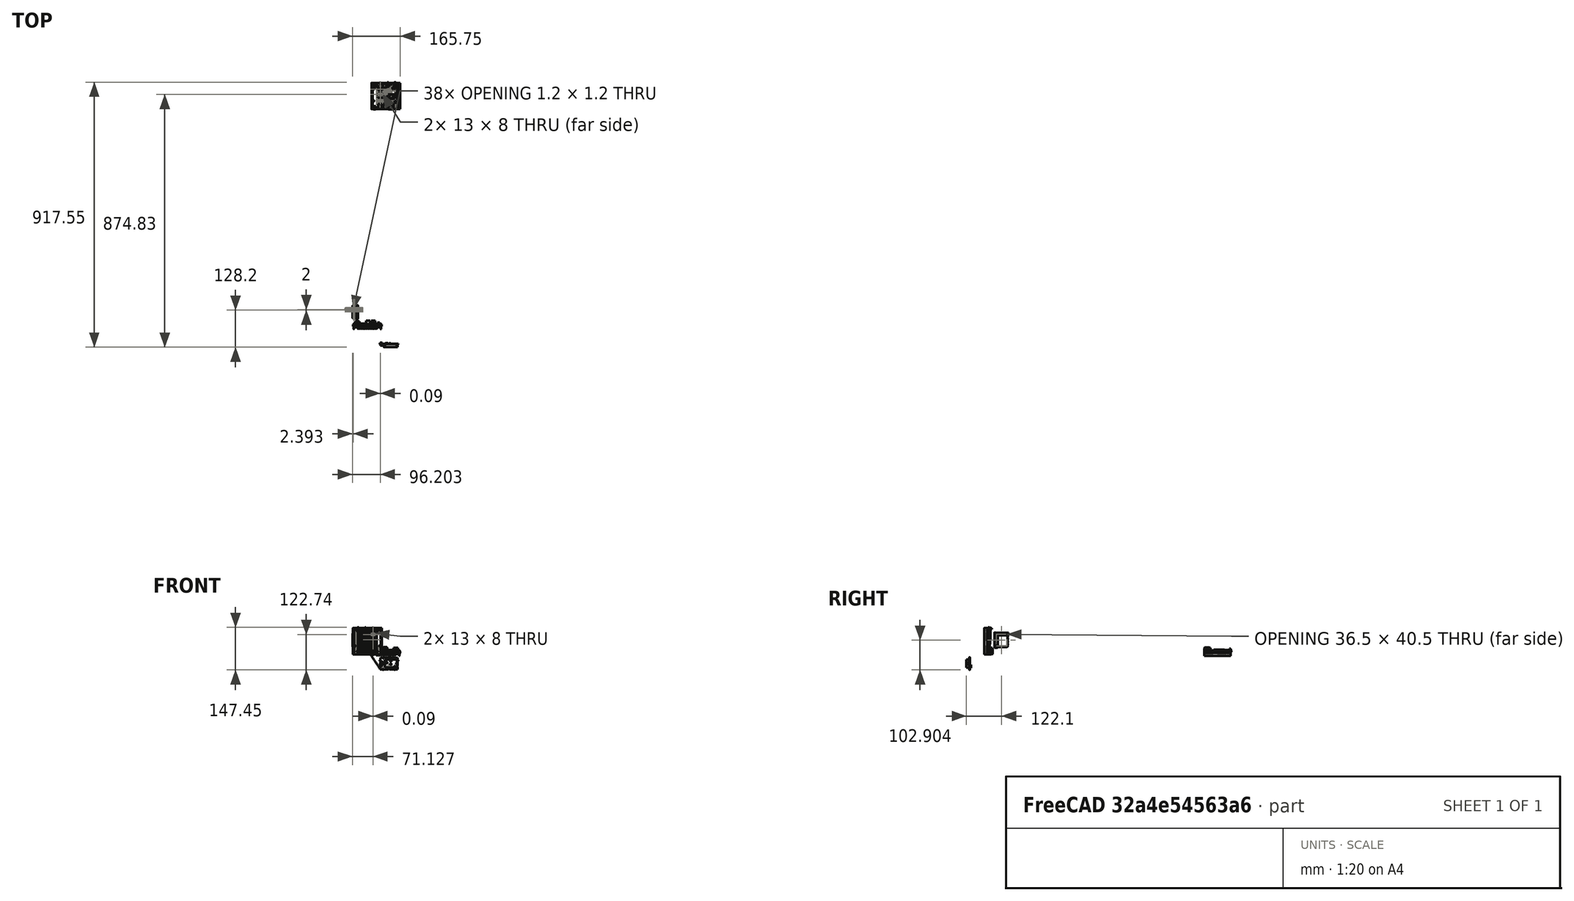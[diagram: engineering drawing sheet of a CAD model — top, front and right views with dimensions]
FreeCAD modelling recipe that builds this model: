
FCSTD DOCUMENT  (FreeCAD 0.20R29410 (Git))
Label: ISM
License: All rights reserved
LicenseURL: http://en.wikipedia.org/wiki/All_rights_reserved
objects: Part::Feature×29, Part::Cylinder×18, Part::MultiFuse×9, Part::Fillet×7, Part::Cut×6, Part::Extrusion×5, App::Part×4, Part::Box×3, Sketcher::SketchObject×3, Part::Part2DObjectPython×2
note: 82 computed .brp shape members not serialized (recipe doc carries the construction recipe); baked Part::Feature solids carry a one-line shape summary decoded from their .brp

FEATURE [Part::Box] Box001  label="Cube001"
  AttacherType = Attacher::AttachEngine3D
  Height = 0.1
  Length = 0.1
  Width = 0.1
FEATURE [Part::Feature] Part__Feature007  label="Heat Sink"
  shape: bbox 100 x 91 x 19 mm, 161 faces (baked)
FEATURE [Part::Feature] Part__Feature008  label="Battery Holder"
  shape: bbox 28.5 x 16 x 6 mm, 91 faces (baked)
FEATURE [Part::Feature] Part__Feature009  label="DC Jack"
  shape: bbox 7.6 x 11.5 x 9.75 mm, 10 faces (baked)
FEATURE [Part::Feature] Part__Feature010  label="PCB"
  shape: bbox 90 x 90 x 3.3 mm, 59 faces (baked)
FEATURE [Part::Feature] Part__Feature011  label="HDMI"
  shape: bbox 14.51 x 11.61 x 5.506 mm, 31 faces (baked)
FEATURE [Part::Feature] Part__Feature012  label="Ethernet"
  shape: bbox 15.9 x 21.4 x 13.5 mm, 25 faces (baked)
FEATURE [Part::Feature] Part__Feature013  label="USB 3.0 B"
  shape: bbox 14.55 x 17.5 x 16.15 mm, 36 faces (baked)
FEATURE [Part::Feature] Part__Feature014  label="USB 3.0 A"
  shape: bbox 14.55 x 17.5 x 16.15 mm, 36 faces (baked)
FEATURE [Part::Feature] Part__Feature015  label="Audio Jack"
  shape: bbox 6.5 x 14 x 4 mm, 10 faces (baked)
FEATURE [Part::Feature] Part__Feature016  label="Fan Plug"
  shape: bbox 3.75 x 7.5 x 4.75 mm, 32 faces (baked)
FEATURE [Part::Feature] Part__Feature017  label="REMOCON"
  shape: bbox 7.006 x 5.006 x 12.01 mm, 30 faces (baked)
FEATURE [Part::Feature] Part__Feature018  label="eMMC"
  shape: bbox 13.5 x 18.5 x 2.8 mm, 33 faces (baked)
FEATURE [Part::Feature] Part__Feature019  label="MicroUSB"
  shape: bbox 7.012 x 4.616 x 3.511 mm, 31 faces (baked)
FEATURE [Part::Feature] Part__Feature020  label="Switch"
  shape: bbox 9 x 5.74 x 3.5 mm, 11 faces (baked)
FEATURE [Part::Feature] Part__Feature021  label="MicroSD Card Socket"
  shape: bbox 11.5 x 5.5 x 3.5 mm, 11 faces (baked)
FEATURE [Part::Feature] Part__Feature022  label="7 Pin Header"
  shape: bbox 17.5 x 2.5 x 8 mm, 41 faces (baked)
FEATURE [Part::Feature] Part__Feature023  label="UART"
  shape: bbox 5 x 12.5 x 6 mm, 43 faces (baked)
FEATURE [Part::Feature] Part__Feature024  label="40 Pin Header"
  shape: bbox 5 x 50 x 8 mm, 206 faces (baked)
FEATURE [App::Part] Odroid_N2__v4  label="Odroid-N2+ v4"
  Group = -> [Part__Feature007,Part__Feature008,Part__Feature009,Part__Feature010,Part__Feature011,Part__Feature012,Part__Feature013,Part__Feature014,Part__Feature015,Part__Feature016,Part__Feature017,Part__Feature018,Part__Feature019,Part__Feature020,Part__Feature021,Part__Feature022,Part__Feature023,Part__Feature024]
  Origin = -> Origin002
  Placement = pos=(31,-814,-44.46) rot=(0,0,1;0rad)
FEATURE [Part::MultiFuse] Fusion001  label="odroidN2"
  Placement = pos=(5,50,52) rot=(0,0.707107,0.707107;3.14159rad)
  Shapes = -> [Box001,Odroid_N2__v4]
FEATURE [Sketcher::SketchObject] Sketch
  FullyConstrained = true
  sketch-geometry (28):
    g0: LineSegment StartX=-93.25 StartY=70.6 StartZ=0 EndX=-93.25 EndY=67.6 EndZ=0
    g1: LineSegment StartX=-93.25 StartY=67.6 StartZ=0 EndX=-95.25 EndY=67.6 EndZ=0
    g2: LineSegment StartX=-95.25 StartY=67.6 StartZ=0 EndX=-95.25 EndY=65.8 EndZ=0
    g3: LineSegment StartX=-95.25 StartY=65.8 StartZ=0 EndX=-93.25 EndY=65.8 EndZ=0
    g4: LineSegment StartX=-93.25 StartY=65.8 StartZ=0 EndX=-93.25 EndY=64.3 EndZ=0
    g5: LineSegment StartX=-93.25 StartY=64.3 StartZ=0 EndX=-95.25 EndY=64.3 EndZ=0
    g6: LineSegment StartX=-95.25 StartY=64.3 StartZ=0 EndX=-95.25 EndY=62.5 EndZ=0
    g7: LineSegment StartX=-95.25 StartY=62.5 StartZ=0 EndX=-93.25 EndY=62.5 EndZ=0
    g8: LineSegment StartX=-93.25 StartY=62.5 StartZ=0 EndX=-93.25 EndY=59.5 EndZ=0
    g9: LineSegment StartX=-93.25 StartY=59.5 StartZ=0 EndX=-97.25 EndY=59.5 EndZ=0
    g10: LineSegment StartX=-97.25 StartY=59.5 StartZ=0 EndX=-97.25 EndY=87.6 EndZ=0
    g11: LineSegment StartX=-97.25 StartY=87.6 StartZ=0 EndX=7.25 EndY=87.6 EndZ=0
    g12: LineSegment StartX=7.25 StartY=87.6 StartZ=0 EndX=7.25 EndY=59.5 EndZ=0
    g13: LineSegment StartX=7.25 StartY=59.5 StartZ=0 EndX=3.25 EndY=59.5 EndZ=0
    g14: LineSegment StartX=3.25 StartY=59.5 StartZ=0 EndX=3.25 EndY=62.5 EndZ=0
    g15: LineSegment StartX=3.25 StartY=62.5 StartZ=0 EndX=5.25 EndY=62.5 EndZ=0
    g16: LineSegment StartX=5.25 StartY=62.5 StartZ=0 EndX=5.25 EndY=64.3 EndZ=0
    g17: LineSegment StartX=5.25 StartY=64.3 StartZ=0 EndX=3.25 EndY=64.3 EndZ=0
    g18: LineSegment StartX=3.25 StartY=64.3 StartZ=0 EndX=3.25 EndY=65.8 EndZ=0
    g19: LineSegment StartX=3.25 StartY=65.8 StartZ=0 EndX=5.25 EndY=65.8 EndZ=0
    g20: LineSegment StartX=5.25 StartY=65.8 StartZ=0 EndX=5.25 EndY=67.6 EndZ=0
    g21: LineSegment StartX=5.25 StartY=67.6 StartZ=0 EndX=3.25 EndY=67.6 EndZ=0
    g22: LineSegment StartX=3.25 StartY=67.6 StartZ=0 EndX=3.25 EndY=70.6 EndZ=0
    g23: LineSegment StartX=3.25 StartY=70.6 StartZ=0 EndX=5.25 EndY=70.6 EndZ=0
    g24: LineSegment StartX=5.25 StartY=70.6 StartZ=0 EndX=5.25 EndY=85.6 EndZ=0
    g25: LineSegment StartX=5.25 StartY=85.6 StartZ=0 EndX=-95.25 EndY=85.6 EndZ=0
    g26: LineSegment StartX=-95.25 StartY=85.6 StartZ=0 EndX=-95.25 EndY=70.6 EndZ=0
    g27: LineSegment StartX=-95.25 StartY=70.6 StartZ=0 EndX=-93.25 EndY=70.6 EndZ=0
  constraints (84):
    c: Vertical(g0)
    c: Coincident(g1,g0)
    c: Horizontal(g3)
    c: Coincident(g6,g5)
    c: Coincident(g7,g6)
    c: Coincident(g8,g7)
    c: Vertical(g8)
    c: Coincident(g9,g8)
    c: Vertical(g10)
    c: Horizontal(g11)
    c: Vertical(g12)
    c: Coincident(g14,g13)
    c: Coincident(g16,g15)
    c: Vertical(g16)
    c: Coincident(g17,g16)
    c: Coincident(g20,g19)
    c: Vertical(g20)
    c: Coincident(g21,g20)
    c: Coincident(g22,g21)
    c: Horizontal(g25)
    c: Vertical(g26)
    c: Coincident(g27,g0)
    c: Horizontal(g27)
    c: Coincident(g11,g12)
    c: Horizontal(g9)
    c: Horizontal(g7)
    c: Horizontal(g5)
    c: Vertical(g6)
    c: Vertical(g4)
    c: Vertical(g2)
    c: Horizontal(g1)
    c: Coincident(g2,g1)
    c: Coincident(g3,g2)
    c: Vertical(g18)
    c: Vertical(g14)
    c: Vertical(g22)
    c: Coincident(g22,g23)
    c: Vertical(g24)
    c: Coincident(g24,g25)
    c: Coincident(g10,g9)
    c: Coincident(g4,g5)
    c: Coincident(g14,g15)
    c: Coincident(g18,g19)
    c: Horizontal(g23)
    c: Horizontal(g21)
    c: Horizontal(g19)
    c: Horizontal(g17)
    c: Horizontal(g15)
    c: Coincident(g23,g24)
    c: DistanceX(g10,g25) = 2
    c: Coincident(g25,g26)
    c: Coincident(g11,g10)
    c: DistanceY(g25,g10) = 2
    c: DistanceY(g8,g7) = 3
    c: DistanceX(g5,g4) = 2
    c: Coincident(g3,g4)
    c: DistanceX(g7,g3) = 0
    c: DistanceX(g0,g3) = 0
    c: DistanceX(g2,g3) = 2
    c: DistanceX(g7) = -93.25
    c: DistanceY(g7) = 62.5
    c: DistanceY(g7,g4) = 1.8
    c: DistanceY(g4,g3) = 1.5
    c: DistanceY(g3,g0) = 1.8
    c: DistanceY(g0,g0) = 3
    c: Coincident(g27,g26)
    c: DistanceY(g26,g25) = 15
    c: DistanceX(g9,g6) = 2
    c: DistanceY(g13,g8) = 0
    c: DistanceY(g14,g6) = 0
    c: DistanceY(g5,g17) = 0
    c: DistanceY(g18,g2) = 0
    c: DistanceY(g0,g21) = 0
    c: DistanceY(g0,g22) = 0
    c: DistanceX(g7,g14) = 96.5
    c: Coincident(g17,g18)
    c: Horizontal(g13)
    c: Coincident(g12,g13)
    c: DistanceX(g17,g14) = 0
    c: DistanceX(g18,g21) = 0
    c: DistanceX(g16,g19) = 0
    c: DistanceX(g23,g20) = 0
    c: DistanceX(g24,g11) = 2
    c: DistanceX(g21,g20) = 2
FEATURE [Part::Extrusion] Extrude
  Base = -> Sketch
  Dir = (0,0,1)
  DirMode = 2
  FaceMakerClass = Part::FaceMakerBullseye
  LengthFwd = 100
  LengthRev = 0
  Placement = pos=(0,0,50) rot=(0,0,1;0rad)
  Solid = true
  Symmetric = false
FEATURE [Part::Feature] Part__Feature  label="ips7100s"
  Placement = pos=(-83,90,125) rot=(0.57735,0.57735,0.57735;4.18879rad)
  shape: bbox 13.98 x 44.07 x 48.08 mm, 1935 faces (baked)
FEATURE [Part::Feature] Part__Feature025  label="Grove Connector (flat) v1"
  Placement = pos=(7.6,-5,15) rot=(0.57735,-0.57735,0.57735;2.0944rad)
  shape: bbox 9.95 x 5 x 12 mm, 192 faces (baked)
FEATURE [Part::Feature] Part__Feature026  label="96877A110"
  Placement = pos=(0.192171,-12.0856,4.84238) rot=(1,0,0;1.5708rad)
  shape: bbox 4.369 x 3.345 x 4.369 mm, 39 faces (baked)
FEATURE [Part::Feature] Part__Feature027  label="96877A110(Mirror)"
  Placement = pos=(72.4078,-12.0856,4.84238) rot=(0,0.707107,0.707107;3.14159rad)
  shape: bbox 4.369 x 3.345 x 4.369 mm, 39 faces (baked)
FEATURE [Part::Feature] Part__Feature028  label="96877A111"
  Placement = pos=(0.192171,4.0856,35.1576) rot=(-1,0,0;1.5708rad)
  shape: bbox 4.369 x 3.345 x 4.369 mm, 39 faces (baked)
FEATURE [Part::Feature] Part__Feature029  label="96877A110(Mirror) (1)"
  Placement = pos=(72.4078,4.0856,35.1576) rot=(0,0.707107,-0.707107;3.14159rad)
  shape: bbox 4.369 x 3.345 x 4.369 mm, 39 faces (baked)
FEATURE [Part::Feature] Part__Feature030  label="COMPOUND"
  shape: bbox 64 x 15 x 44 mm, 74 faces, 8 solids (baked)
FEATURE [App::Part] Seed_Grove_SCD30_v19  label="Seed Grove SCD30 v19"
  Group = -> [Part__Feature025,Part__Feature026,Part__Feature027,Part__Feature028,Part__Feature029,Part__Feature030]
  Origin = -> Origin
  Placement = pos=(-3,92.5,130) rot=(0.57735,-0.57735,-0.57735;4.18879rad)
FEATURE [Part::Feature] Part__Feature033  label="Grove_1x4 v002"
  Placement = pos=(6.76256,6.01631,15.2463) rot=(-0.57735,0.57735,0.57735;2.0944rad)
  shape: bbox 9.95 x 5 x 12 mm, 192 faces (baked)
FEATURE [Part::Feature] Part__Feature035  label="Grove_1x4 v003"
  Placement = pos=(6.76256,6.01631,15.2463) rot=(-0.57735,0.57735,0.57735;2.0944rad)
  shape: bbox 9.95 x 5 x 12 mm, 192 faces (baked)
FEATURE [Part::Feature] Part__Feature036  label="SOLID002"
  shape: bbox 41.9 x 4.1 x 23.8 mm, 29 faces (baked)
FEATURE [App::Part] Grove_AK9753_v014  label="BME280"
  Group = -> [Part__Feature035,Part__Feature036]
  Origin = -> Origin005
  Placement = pos=(-19,93,56) rot=(-0.57735,-0.57735,0.57735;2.0944rad)
FEATURE [Part::Feature] Part__Feature034  label="SOLID001"
  shape: bbox 41.9 x 4.1 x 23.8 mm, 29 faces (baked)
FEATURE [App::Part] Grove_AK9753_v013  label="BME680"
  Group = -> [Part__Feature033,Part__Feature034]
  Origin = -> Origin004
  Placement = pos=(-43,93,56) rot=(-0.57735,-0.57735,0.57735;2.0944rad)
FEATURE [Part::Cylinder] Cylinder
  Angle = 360
  AttacherType = Attacher::AttachEngine3D
  FirstAngle = 0
  Height = 4
  Placement = pos=(-45,106,102) rot=(-1,0,0;1.5708rad)
  Radius = 8
  SecondAngle = 0
FEATURE [Part::Cylinder] Cylinder001
  Angle = 360
  AttacherType = Attacher::AttachEngine3D
  FirstAngle = 0
  Height = 4
  Placement = pos=(-45,106,102) rot=(-1,0,0;1.5708rad)
  Radius = 3.25
  SecondAngle = 0
FEATURE [Part::Cut] Cut  label="micHolder"
  Base = -> Cylinder
  Tool = -> Cylinder001
FEATURE [Part::Cylinder] Cylinder002
  Angle = 360
  AttacherType = Attacher::AttachEngine3D
  FirstAngle = 0
  Height = 18.5
  Placement = pos=(-45,87.5,102) rot=(-1,0,0;1.5708rad)
  Radius = 8
  SecondAngle = 0
FEATURE [Part::Cylinder] Cylinder003
  Angle = 360
  AttacherType = Attacher::AttachEngine3D
  FirstAngle = 0
  Height = 18.5
  Placement = pos=(-45,87.5,102) rot=(-1,0,0;1.5708rad)
  Radius = 5
  SecondAngle = 0
FEATURE [Part::Cut] Cut001
  Base = -> Cylinder002
  Tool = -> Cylinder003
FEATURE [Part::MultiFuse] Fusion
  Shapes = -> [Cut,Cut001]
FEATURE [Part::Box] Box  label="Cube"
  AttacherType = Attacher::AttachEngine3D
  Height = 6
  Length = 16
  Placement = pos=(-48,87.5,118) rot=(0,1,0;1.5708rad)
  Width = 23
FEATURE [Part::Cut] Cut002
  Base = -> Fusion
  Tool = -> Box
FEATURE [Sketcher::SketchObject] Sketch001
  FullyConstrained = true
  Placement = pos=(0,0,0) rot=(0.57735,0.57735,0.57735;2.0944rad)
  sketch-geometry (6):
    g0: LineSegment StartX=135.5 StartY=127 StartZ=0 EndX=87.5 EndY=127 EndZ=0
    g1: LineSegment StartX=87.5 StartY=127 StartZ=0 EndX=87.5 EndY=75 EndZ=0
    g2: LineSegment StartX=87.5 StartY=75 StartZ=0 EndX=99.5 EndY=75 EndZ=0
    g3: LineSegment StartX=99.5 StartY=75 StartZ=0 EndX=99.5 EndY=117 EndZ=0
    g4: LineSegment StartX=99.5 StartY=117 StartZ=0 EndX=135.5 EndY=117 EndZ=0
    g5: LineSegment StartX=135.5 StartY=117 StartZ=0 EndX=135.5 EndY=127 EndZ=0
  constraints (18):
    c: Horizontal(g0)
    c: Coincident(g1,g0)
    c: Vertical(g1)
    c: Vertical(g3)
    c: Coincident(g4,g3)
    c: Horizontal(g4)
    c: Coincident(g5,g4)
    c: Coincident(g5,g0)
    c: Vertical(g5)
    c: Horizontal(g2)
    c: Coincident(g2,g3)
    c: DistanceY(g1,g0) = 52
    c: Coincident(g2,g1)
    c: DistanceX(g1,g2) = 12
    c: DistanceX(g0) = 87.5
    c: DistanceY(g4,g0) = 10
    c: DistanceY(g0) = 127
    c: DistanceX(g0,g0) = 48
FEATURE [Part::Extrusion] Extrude001
  Base = -> Sketch001
  Dir = (1,0,0)
  DirMode = 2
  FaceMakerClass = Part::FaceMakerBullseye
  LengthFwd = 5
  LengthRev = 0
  Placement = pos=(-82.5,0,0) rot=(0,0,1;0rad)
  Solid = true
  Symmetric = false
FEATURE [Part::Box] Box002  label="Cube002"
  AttacherType = Attacher::AttachEngine3D
  Height = 5
  Length = 54
  Placement = pos=(-67.5,87.5,56) rot=(0,0,1;0rad)
  Width = 20
FEATURE [Sketcher::SketchObject] Sketch002
  FullyConstrained = true
  Placement = pos=(0,0,0) rot=(0.57735,0.57735,0.57735;2.0944rad)
  sketch-geometry (6):
    g0: LineSegment StartX=87.5 StartY=125 StartZ=0 EndX=97.5 EndY=125 EndZ=0
    g1: LineSegment StartX=97.5 StartY=125 StartZ=0 EndX=97.5 EndY=75 EndZ=0
    g2: LineSegment StartX=97.5 StartY=75 StartZ=0 EndX=127.5 EndY=75 EndZ=0
    g3: LineSegment StartX=127.5 StartY=65 StartZ=0 EndX=87.5 EndY=65 EndZ=0
    g4: LineSegment StartX=87.5 StartY=65 StartZ=0 EndX=87.5 EndY=125 EndZ=0
    g5: LineSegment StartX=127.5 StartY=65 StartZ=0 EndX=127.5 EndY=75 EndZ=0
  constraints (18):
    c: Horizontal(g0)
    c: Coincident(g0,g1)
    c: Vertical(g1)
    c: Coincident(g1,g2)
    c: Horizontal(g2)
    c: Horizontal(g3)
    c: Coincident(g3,g4)
    c: Coincident(g4,g0)
    c: Vertical(g4)
    c: Coincident(g5,g3)
    c: Coincident(g5,g2)
    c: Vertical(g5)
    c: DistanceX(g3) = 87.5
    c: DistanceY(g3) = 65
    c: DistanceY(g3,g0) = 60
    c: DistanceX(g0,g0) = 10
    c: DistanceX(g1,g2) = 30
    c: DistanceY(g3,g2) = 10
FEATURE [Part::Extrusion] Extrude002
  Base = -> Sketch002
  Dir = (1,0,0)
  DirMode = 2
  FaceMakerClass = Part::FaceMakerBullseye
  LengthFwd = 5
  LengthRev = 0
  Placement = pos=(-10,0,0) rot=(0,0,1;0rad)
  Solid = true
  Symmetric = false
FEATURE [Part::MultiFuse] Fusion002
  Shapes = -> [Extrude,Cut002,Extrude001,Box002,Extrude002]
FEATURE [Part::Cylinder] Cylinder004
  Angle = 360
  AttacherType = Attacher::AttachEngine3D
  FirstAngle = 0
  Height = 4
  Placement = pos=(-45,85.5,86) rot=(-1,0,0;1.5708rad)
  Radius = 0.5
  SecondAngle = 0
FEATURE [Part::Cut] Cut003
  Base = -> Fusion002
  Tool = -> Cylinder004
FEATURE [Part::Cylinder] Cylinder005
  Angle = 360
  AttacherType = Attacher::AttachEngine3D
  FirstAngle = 0
  Height = 10
  Placement = pos=(-78,93.6,80.6) rot=(0,-1,0;1.5708rad)
  Radius = 1.15
  SecondAngle = 0
FEATURE [Part::Cylinder] Cylinder006
  Angle = 360
  AttacherType = Attacher::AttachEngine3D
  FirstAngle = 0
  Height = 10
  Placement = pos=(-78,130.4,121.4) rot=(0,-1,0;1.5708rad)
  Radius = 1.15
  SecondAngle = 0
FEATURE [Part::MultiFuse] Fusion003
  Placement = pos=(1.2,0,0) rot=(0,0,1;0rad)
  Shapes = -> [Cylinder006,Cylinder005]
FEATURE [Part::Cylinder] Cylinder007
  Angle = 360
  AttacherType = Attacher::AttachEngine3D
  FirstAngle = 0
  Height = 10
  Placement = pos=(-1.5,92.5,120) rot=(0,-1,0;1.5708rad)
  Radius = 1.15
  SecondAngle = 0
FEATURE [Part::Cylinder] Cylinder008
  Angle = 360
  AttacherType = Attacher::AttachEngine3D
  FirstAngle = 0
  Height = 10
  Placement = pos=(-1.5,92.5,80) rot=(0,-1,0;1.5708rad)
  Radius = 1.15
  SecondAngle = 0
FEATURE [Part::Cylinder] Cylinder009
  Angle = 360
  AttacherType = Attacher::AttachEngine3D
  FirstAngle = 0
  Height = 10
  Placement = pos=(-1.5,122.5,70) rot=(0,-1,0;1.5708rad)
  Radius = 1.15
  SecondAngle = 0
FEATURE [Part::MultiFuse] Fusion004
  Shapes = -> [Cylinder007,Cylinder008,Cylinder009]
FEATURE [Part::Cylinder] Cylinder010
  Angle = 360
  AttacherType = Attacher::AttachEngine3D
  FirstAngle = 0
  Height = 10
  Placement = pos=(-63,102.1,21.9) rot=(0,0,1;0rad)
  Radius = 1.15
  SecondAngle = 0
FEATURE [Part::Cylinder] Cylinder011
  Angle = 360
  AttacherType = Attacher::AttachEngine3D
  FirstAngle = 0
  Height = 10
  Placement = pos=(-43,102.1,21.9) rot=(0,0,1;0rad)
  Radius = 1.15
  SecondAngle = 0
FEATURE [Part::Cylinder] Cylinder012
  Angle = 360
  AttacherType = Attacher::AttachEngine3D
  FirstAngle = 0
  Height = 10
  Placement = pos=(-39,102.1,21.9) rot=(0,0,1;0rad)
  Radius = 1.15
  SecondAngle = 0
FEATURE [Part::Cylinder] Cylinder013
  Angle = 360
  AttacherType = Attacher::AttachEngine3D
  FirstAngle = 0
  Height = 10
  Placement = pos=(-19,102.1,21.9) rot=(0,0,1;0rad)
  Radius = 1.15
  SecondAngle = 0
FEATURE [Part::MultiFuse] Fusion005
  Placement = pos=(0,0,31.17) rot=(0,0,1;0rad)
  Shapes = -> [Cylinder013,Cylinder010,Cylinder011,Cylinder012]
FEATURE [Part::MultiFuse] Fusion006
  Shapes = -> [Fusion005,Fusion003,Fusion004]
FEATURE [Part::Cut] Cut004  label="n2Hold"
  Base = -> Cut003
  Tool = -> Fusion006
FEATURE [Part::Cylinder] Cylinder014
  Angle = 360
  AttacherType = Attacher::AttachEngine3D
  FirstAngle = 0
  Height = 4
  Placement = pos=(-29.24,85.5,53) rot=(0,0.707107,0.707107;3.14159rad)
  Radius = 2.5
  SecondAngle = 0
FEATURE [Part::Cylinder] Cylinder015
  Angle = 360
  AttacherType = Attacher::AttachEngine3D
  FirstAngle = 0
  Height = 4
  Placement = pos=(-53.23,85.5,53) rot=(0,0.707107,0.707107;3.14159rad)
  Radius = 2.5
  SecondAngle = 0
FEATURE [Part::Cylinder] Cylinder016
  Angle = 360
  AttacherType = Attacher::AttachEngine3D
  FirstAngle = 0
  Height = 4
  Placement = pos=(-1,85.5,130.99) rot=(-1,0,0;1.5708rad)
  Radius = 2.5
  SecondAngle = 0
FEATURE [Part::Cylinder] Cylinder017
  Angle = 360
  AttacherType = Attacher::AttachEngine3D
  FirstAngle = 0
  Height = 4
  Placement = pos=(-88,85.5,91.28) rot=(-1,0,0;1.5708rad)
  Radius = 2.5
  SecondAngle = 0
FEATURE [Part::MultiFuse] Fusion007
  Shapes = -> [Cylinder014,Cylinder015,Cylinder016,Cylinder017]
FEATURE [Part::Cut] Cut005
  Base = -> Cut004
  Tool = -> Fusion007
FEATURE [Part::Part2DObjectPython] ShapeString  # Draft 2D object (typed FeaturePython)
  FontFile = <userpath>/gitHubRepos/3DMints2022/mslns/fonts/afta-sans/AftaSansThin-Regular.otf
  MakeFace = true
  Placement = pos=(-126.59,62.91,93.07) rot=(0,-1,0;1.5708rad)
  Size = 5
  String = MINTS-AI
  Tracking = 0
FEATURE [Part::Extrusion] Extrude003
  Base = -> ShapeString
  Dir = (-1,0,-3e-16)
  DirMode = 2
  FaceMakerClass = Part::FaceMakerBullseye
  LengthFwd = 2
  LengthRev = 0
  Placement = pos=(29.5,0,5) rot=(0,0,1;0rad)
  Solid = false
  Symmetric = false
FEATURE [Part::Part2DObjectPython] ShapeString001  # Draft 2D object (typed FeaturePython)
  FontFile = <userpath>/gitHubRepos/3DMints2022/mslns/fonts/afta-sans/AftaSansThin-Regular.otf
  MakeFace = true
  Placement = pos=(-126.59,62.91,93.07) rot=(0,-1,0;1.5708rad)
  Size = 5
  String = MINTS-AI
  Tracking = 0
FEATURE [Part::Extrusion] Extrude004
  Base = -> ShapeString001
  Dir = (-1,0,-3e-16)
  DirMode = 2
  FaceMakerClass = Part::FaceMakerBullseye
  LengthFwd = 2
  LengthRev = 0
  Placement = pos=(-119.5,0,195) rot=(0,1,0;3.14159rad)
  Solid = false
  Symmetric = false
FEATURE [Part::MultiFuse] Fusion008  label="n2Hold001"
  Shapes = -> [Cut005,Extrude003,Extrude004]
FEATURE [Part::Fillet] Fillet
  Base = -> Fusion008
  Edges = 8 edges: [Edge61 r=2,Edge68 r=1,Edge69 r=1,Edge70 r=2,Edge138 r=2,Edge162 r=1,Edge230 r=1,Edge241 r=2]
FEATURE [Part::Fillet] Fillet001
  Base = -> Fillet
  Edges = 10 edges r=1: [Edge29,Edge30,Edge31,Edge32,Edge33,Edge53,Edge124,Edge127,Edge155,Edge159]
FEATURE [Part::Fillet] Fillet002
  Base = -> Fillet001
  Edges = 3 edges r=1: [Edge229,Edge234,Edge235]
FEATURE [Part::Fillet] Fillet003
  Base = -> Fillet002
  Edges = 14 edges r=1.5: [Edge12,Edge13,Edge14,Edge15,Edge17,Edge18,Edge22,Edge23,Edge24,Edge25,Edge26,Edge27,Edge28,Edge29]
FEATURE [Part::Fillet] Fillet004
  Base = -> Fillet003
  Edges = 36 edges r=1.5: [Edge110,Edge111,Edge113,Edge152,Edge153,Edge226,Edge227,Edge262,Edge349,Edge350,Edge351,Edge352,Edge353,Edge354,Edge355,Edge359,Edge360,Edge361,Edge362,Edge366,Edge697,Edge698,Edge754,Edge755,Edge756,Edge757,Edge758,Edge761,Edge762,Edge763,Edge764,Edge765,Edge766,Edge767,Edge770,Edge771]
FEATURE [Part::Fillet] Fillet005
  Base = -> Fillet004
  Edges = 2 edges r=2: [Edge376,Edge378]
FEATURE [Part::Fillet] Fillet006
  Base = -> Fillet005
  Edges = 14 edges r=0.5: [Edge1,Edge2,Edge3,Edge4,Edge8,Edge18,Edge20,Edge21,Edge24,Edge51,Edge52,Edge57,Edge58,Edge59]
